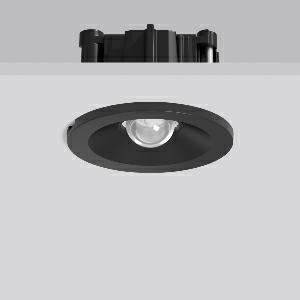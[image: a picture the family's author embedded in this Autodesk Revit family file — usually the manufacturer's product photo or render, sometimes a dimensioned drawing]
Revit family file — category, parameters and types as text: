
# Revit family: turia_l_672411_003_89_ce98
name_source: partatom
category: Lighting Fixtures
units: mm (PartAtom-declared; Revit-internal decimal feet)

## family parameters
Cut with Voids When Loaded = No
Host = Face
Light Source = No
Part Type = Normal
Room Calculation Point = No
Round Connector Dimension = Use Diameter
Shared = No

## types (1)
- TURIA L (1 x LED Modul 765, 220 lm, 6500)
    Apparent Load = 5 VA
    CIE Flux Codes = 18 55 97 100 100
    Color Rendering = 70
    Color Temperature = 6500
    Default Elevation = 1800 mm
    Description = Series: TURIA L
Round emergency luminaire for escape route lighting. With plastic lenses for area lighting. Suitable for connection to central battery systems. With MOM monitoring module for LPS (Low Power Supply) small central battery units of the type Easy+IP. With enclosed separate ceiling mounting ring also suitable for ceiling cut-outs of Ø 68 mm. 
Colour: black
Diameter: 62 mm
Height: 3 mm
Cut-out diameter: 54-68 mm
Recess height: 76-162 mm
Luminaire: recess height: 42 mm
Weight: 350 g
Operating mode: non-maintained power mode
Lamp: LED
Socket: without socket
Colour temperature: 6500K
Colour rendering index (CRI): 70
System power: 4.8 W
Rated luminous flux: 220 lm
Luminous flux, emergency: 220 lm
System power, emergency: 4.8 W
Control gear: Regulated power supply
Protection class: II
Type of protection: IP 20
    Height = 0 mm  [stored 0 ft]
    Lamp = 1 x LED Modul 765
    Lamp Light Flux = 220 lm
    Lamp count = 1
    Length = 62 mm  [stored 0.203412 ft]
    Lifetime = 50000 h
    Luminous efficacy = 46 lm/W
    Manufacturer = RZB
    ModVariant = No
    Model = 672411.003.89
    Mounting Place = Ceiling
    Mounting Type = Recessed
    Number of Poles = 1
    OnlyDefault = Yes
    Power Factor = 1
    Product Name = TURIA L
    Product group = Recessed ceiling luminaires
    ProductGroupID = 405
    Protection Class = Protection class II
    Protection Degree = IP 20
    RLX_Detail_Level = 1
    RLX_Emergency_Light_Flux = 220 lm
    RLX_Emergency_Type = 3
    RLX_Emergency_Type_DB = Yes
    RlxData = <blob elided: 38393 chars, md5=0e69fc8e>
    Socket = socket
    Standby Power = 0 W
    System Light Flux = 220 lm
    System Power = 5 W
    Type Comments = Product without accessories
    Type Image = 672412.003.jpg
    URL = http://relux.com
    VarID = ---
    Voltage = 230 V
    Voltage Range = 220-240 V
    Weight = 0.00 kg
    Width = 0 mm  [stored 0 ft]

note: [stored X ft] marks values corroborated as IEEE doubles in the binary element streams (Revit-internal decimal feet)

## geometry (parser evidence)
native form markers: Blend x4, Sweep x10
no freeform markers — native parametric forms only
